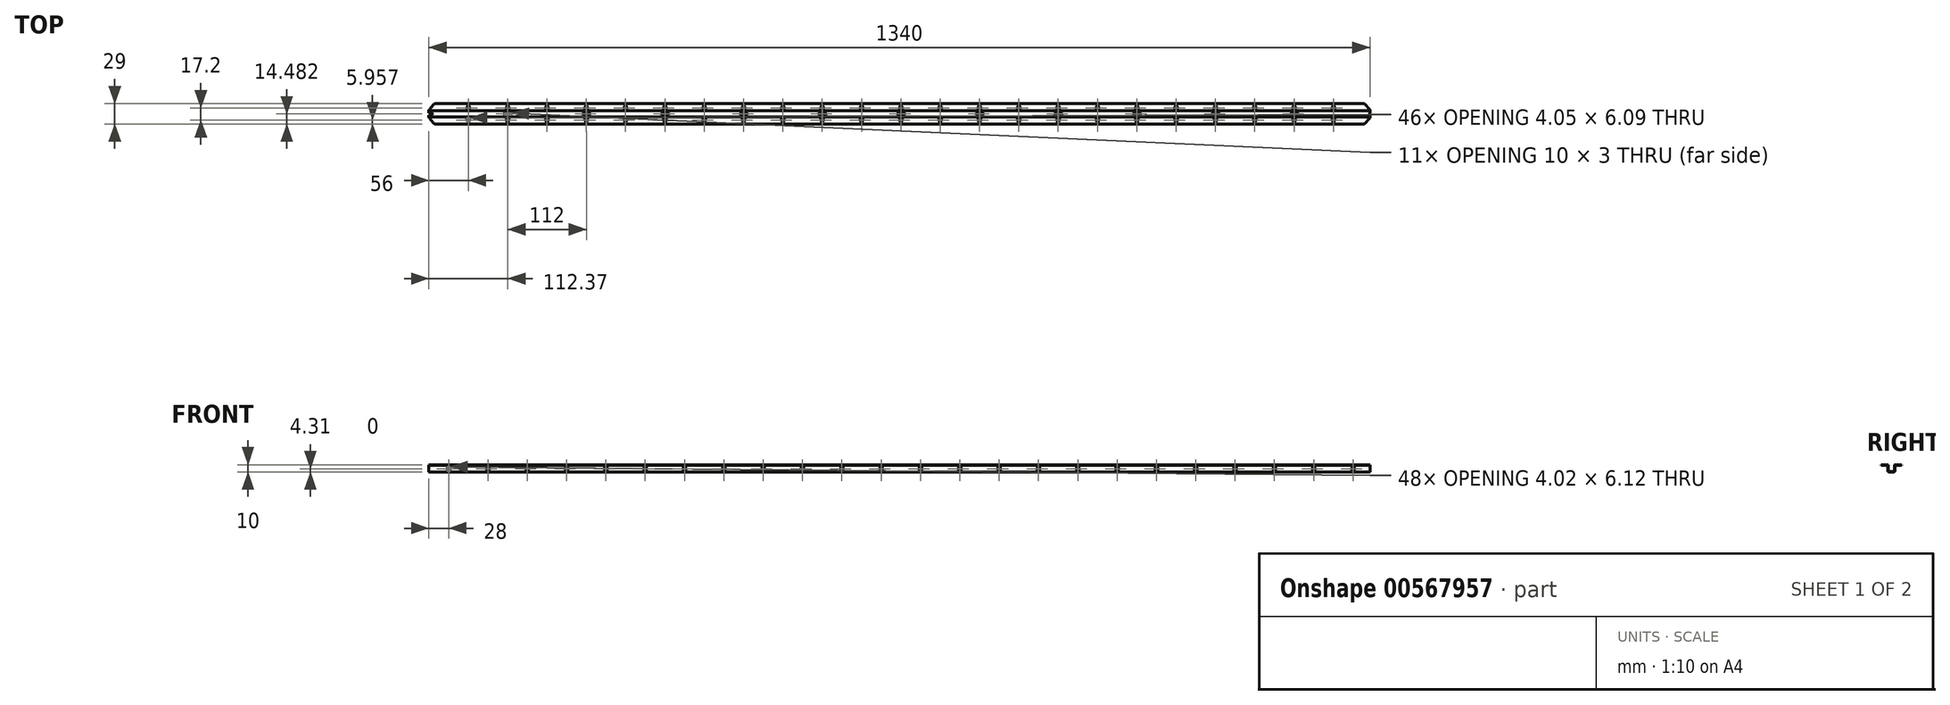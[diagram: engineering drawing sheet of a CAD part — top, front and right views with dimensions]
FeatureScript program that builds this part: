
annotation { "Feature Type Name" : "Feature", "Feature Type Description" : "" }
export const myFeature = defineFeature(function(context is Context, id is Id, definition is map)
    precondition{}
    {
        {
            var Q0;
            Q0=qCreatedBy(makeId("Right.planeOp"),FACE);
            var sketch = newSketch(context, id + "F0", { "sketchPlane" : qUnion([Q0])});
            skLineSegment(sketch, "E0", {"start": v(14.5, 5) * mm, "end": v(5.5, 5) * mm});
            skArc(sketch, "E1", {"start": v(5.5, 5) * mm, "mid": v(4.8, 4.7) * mm, "end": v(4.5, 4) * mm});
            skLineSegment(sketch, "E2", {"start": v(4.5, 4) * mm, "end": v(4.5, -4) * mm});
            skArc(sketch, "E3", {"start": v(4.5, -4) * mm, "mid": v(4.35, -4.35) * mm, "end": v(4, -4.5) * mm});
            skLineSegment(sketch, "E4", {"start": v(4, -4.5) * mm, "end": v(-4, -4.5) * mm});
            skArc(sketch, "E5", {"start": v(-4, -4.5) * mm, "mid": v(-4.35, -4.35) * mm, "end": v(-4.5, -4) * mm});
            skLineSegment(sketch, "E6", {"start": v(-4.5, -4) * mm, "end": v(-4.5, 4) * mm});
            skArc(sketch, "E7", {"start": v(-4.5, 4) * mm, "mid": v(-4.8, 4.7) * mm, "end": v(-5.5, 5) * mm});
            skLineSegment(sketch, "E8", {"start": v(-5.5, 5) * mm, "end": v(-14.5, 5) * mm});
            skLineSegment(sketch, "E9", {"start": v(-14.5, 5) * mm, "end": v(-14.5, 4.5) * mm});
            skLineSegment(sketch, "E10", {"start": v(-14.5, 4.5) * mm, "end": v(-5.5, 4.5) * mm});
            skArc(sketch, "E11", {"start": v(-5.5, 4.5) * mm, "mid": v(-5.15, 4.35) * mm, "end": v(-5, 4) * mm});
            skLineSegment(sketch, "E12", {"start": v(-5, 4) * mm, "end": v(-5, -4) * mm});
            skArc(sketch, "E13", {"start": v(-5, -4) * mm, "mid": v(-4.7, -4.7) * mm, "end": v(-4, -5) * mm});
            skLineSegment(sketch, "E14", {"start": v(-4, -5) * mm, "end": v(4, -5) * mm});
            skArc(sketch, "E15", {"start": v(4, -5) * mm, "mid": v(4.7, -4.7) * mm, "end": v(5, -4) * mm});
            skLineSegment(sketch, "E16", {"start": v(5, -4) * mm, "end": v(5, 4) * mm});
            skArc(sketch, "E17", {"start": v(5, 4) * mm, "mid": v(5.15, 4.35) * mm, "end": v(5.5, 4.5) * mm});
            skLineSegment(sketch, "E18", {"start": v(5.5, 4.5) * mm, "end": v(14.5, 4.5) * mm});
            skLineSegment(sketch, "E19", {"start": v(14.5, 4.5) * mm, "end": v(14.5, 5) * mm});
            skSolve(sketch);
        }
        {
            var Q0;
            Q0 = qSketchRegion(id + "F0", true);
            extrude(context, id + "F1", {"entities" : qUnion([Q0]), "oppositeDirection" : true, "depth" : 1340 * mm, "offsetDistance" : 25 * mm});
        }
        {
            var Q0;
            Q0=makeQuery(id+"F1.opExtrude","SWEPT_FACE",FACE,{"disambiguationData":[OSD([sQuery(id+"F0.wireOp",EDGE,"E4")])]});
            var sketch = newSketch(context, id + "F2", { "sketchPlane" : qUnion([Q0])});
            skLineSegment(sketch, "E20.bottom", {"start": v(-1343.8, -1.5) * mm, "end": v(-1336.2, -1.5) * mm});
            skLineSegment(sketch, "E20.top", {"start": v(-1343.8, 1.5) * mm, "end": v(-1336.2, 1.5) * mm});
            skLineSegment(sketch, "E20.left", {"start": v(-1345, -0.3) * mm, "end": v(-1345, 0.3) * mm});
            skLineSegment(sketch, "E20.right", {"start": v(-1335, -0.3) * mm, "end": v(-1335, 0.3) * mm});
            skArc(sketch, "E21.filletArc", {"start": v(-1345, -0.3) * mm, "mid": v(-1344.65, -1.15) * mm, "end": v(-1343.8, -1.5) * mm});
            skArc(sketch, "E22.filletArc", {"start": v(-1343.8, 1.5) * mm, "mid": v(-1344.65, 1.15) * mm, "end": v(-1345, 0.3) * mm});
            skArc(sketch, "E23.filletArc", {"start": v(-1335, 0.3) * mm, "mid": v(-1335.35, 1.15) * mm, "end": v(-1336.2, 1.5) * mm});
            skArc(sketch, "E24.filletArc", {"start": v(-1336.2, -1.5) * mm, "mid": v(-1335.35, -1.15) * mm, "end": v(-1335, -0.3) * mm});
            skLineSegment(sketch, "E25.bottom", {"start": v(-1119.43, -1.52) * mm, "end": v(-1111.83, -1.52) * mm});
            skLineSegment(sketch, "E25.top", {"start": v(-1119.43, 1.48) * mm, "end": v(-1111.83, 1.48) * mm});
            skLineSegment(sketch, "E25.left", {"start": v(-1120.63, -0.32) * mm, "end": v(-1120.63, 0.28) * mm});
            skLineSegment(sketch, "E25.right", {"start": v(-1110.63, -0.32) * mm, "end": v(-1110.63, 0.28) * mm});
            skArc(sketch, "E26.filletArc", {"start": v(-1120.63, -0.32) * mm, "mid": v(-1120.28, -1.17) * mm, "end": v(-1119.43, -1.52) * mm});
            skArc(sketch, "E27.filletArc", {"start": v(-1119.43, 1.48) * mm, "mid": v(-1120.28, 1.13) * mm, "end": v(-1120.63, 0.28) * mm});
            skArc(sketch, "E28.filletArc", {"start": v(-1110.63, 0.28) * mm, "mid": v(-1110.98, 1.13) * mm, "end": v(-1111.83, 1.48) * mm});
            skArc(sketch, "E29.filletArc", {"start": v(-1111.83, -1.52) * mm, "mid": v(-1110.98, -1.17) * mm, "end": v(-1110.63, -0.32) * mm});
            skLineSegment(sketch, "E30.bottom", {"start": v(-1231.43, -1.52) * mm, "end": v(-1223.83, -1.52) * mm});
            skLineSegment(sketch, "E30.top", {"start": v(-1231.43, 1.48) * mm, "end": v(-1223.83, 1.48) * mm});
            skLineSegment(sketch, "E30.left", {"start": v(-1232.63, -0.32) * mm, "end": v(-1232.63, 0.28) * mm});
            skLineSegment(sketch, "E30.right", {"start": v(-1222.63, -0.32) * mm, "end": v(-1222.63, 0.28) * mm});
            skArc(sketch, "E31.filletArc", {"start": v(-1232.63, -0.32) * mm, "mid": v(-1232.28, -1.17) * mm, "end": v(-1231.43, -1.52) * mm});
            skArc(sketch, "E32.filletArc", {"start": v(-1231.43, 1.48) * mm, "mid": v(-1232.28, 1.13) * mm, "end": v(-1232.63, 0.28) * mm});
            skArc(sketch, "E33.filletArc", {"start": v(-1222.63, 0.28) * mm, "mid": v(-1222.98, 1.13) * mm, "end": v(-1223.83, 1.48) * mm});
            skArc(sketch, "E34.filletArc", {"start": v(-1223.83, -1.52) * mm, "mid": v(-1222.98, -1.17) * mm, "end": v(-1222.63, -0.32) * mm});
            skLineSegment(sketch, "E35.bottom", {"start": v(-1007.43, -1.52) * mm, "end": v(-999.83, -1.52) * mm});
            skLineSegment(sketch, "E35.top", {"start": v(-1007.43, 1.48) * mm, "end": v(-999.83, 1.48) * mm});
            skLineSegment(sketch, "E35.left", {"start": v(-1008.63, -0.32) * mm, "end": v(-1008.63, 0.28) * mm});
            skLineSegment(sketch, "E35.right", {"start": v(-998.63, -0.32) * mm, "end": v(-998.63, 0.28) * mm});
            skArc(sketch, "E36.filletArc", {"start": v(-1008.63, -0.32) * mm, "mid": v(-1008.28, -1.17) * mm, "end": v(-1007.43, -1.52) * mm});
            skArc(sketch, "E37.filletArc", {"start": v(-1007.43, 1.48) * mm, "mid": v(-1008.28, 1.13) * mm, "end": v(-1008.63, 0.28) * mm});
            skArc(sketch, "E38.filletArc", {"start": v(-998.63, 0.28) * mm, "mid": v(-998.98, 1.13) * mm, "end": v(-999.83, 1.48) * mm});
            skArc(sketch, "E39.filletArc", {"start": v(-999.83, -1.52) * mm, "mid": v(-998.98, -1.17) * mm, "end": v(-998.63, -0.32) * mm});
            skLineSegment(sketch, "E40.1.0.0", {"start": v(-895.43, -1.52) * mm, "end": v(-887.83, -1.52) * mm});
            skArc(sketch, "E40.1.0.1", {"start": v(-896.63, -0.32) * mm, "mid": v(-896.28, -1.17) * mm, "end": v(-895.43, -1.52) * mm});
            skLineSegment(sketch, "E40.1.0.2", {"start": v(-896.63, -0.32) * mm, "end": v(-896.63, 0.28) * mm});
            skArc(sketch, "E40.1.0.3", {"start": v(-895.43, 1.48) * mm, "mid": v(-896.28, 1.13) * mm, "end": v(-896.63, 0.28) * mm});
            skLineSegment(sketch, "E40.1.0.4", {"start": v(-895.43, 1.48) * mm, "end": v(-887.83, 1.48) * mm});
            skArc(sketch, "E40.1.0.5", {"start": v(-886.63, 0.28) * mm, "mid": v(-886.98, 1.13) * mm, "end": v(-887.83, 1.48) * mm});
            skLineSegment(sketch, "E40.1.0.6", {"start": v(-886.63, -0.32) * mm, "end": v(-886.63, 0.28) * mm});
            skArc(sketch, "E40.1.0.7", {"start": v(-887.83, -1.52) * mm, "mid": v(-886.98, -1.17) * mm, "end": v(-886.63, -0.32) * mm});
            skLineSegment(sketch, "E40.2.0.0", {"start": v(-783.43, -1.52) * mm, "end": v(-775.83, -1.52) * mm});
            skArc(sketch, "E40.2.0.1", {"start": v(-784.63, -0.32) * mm, "mid": v(-784.28, -1.17) * mm, "end": v(-783.43, -1.52) * mm});
            skLineSegment(sketch, "E40.2.0.2", {"start": v(-784.63, -0.32) * mm, "end": v(-784.63, 0.28) * mm});
            skArc(sketch, "E40.2.0.3", {"start": v(-783.43, 1.48) * mm, "mid": v(-784.28, 1.13) * mm, "end": v(-784.63, 0.28) * mm});
            skLineSegment(sketch, "E40.2.0.4", {"start": v(-783.43, 1.48) * mm, "end": v(-775.83, 1.48) * mm});
            skArc(sketch, "E40.2.0.5", {"start": v(-774.63, 0.28) * mm, "mid": v(-774.98, 1.13) * mm, "end": v(-775.83, 1.48) * mm});
            skLineSegment(sketch, "E40.2.0.6", {"start": v(-774.63, -0.32) * mm, "end": v(-774.63, 0.28) * mm});
            skArc(sketch, "E40.2.0.7", {"start": v(-775.83, -1.52) * mm, "mid": v(-774.98, -1.17) * mm, "end": v(-774.63, -0.32) * mm});
            skLineSegment(sketch, "E40.3.0.0", {"start": v(-671.43, -1.52) * mm, "end": v(-663.83, -1.52) * mm});
            skArc(sketch, "E40.3.0.1", {"start": v(-672.63, -0.32) * mm, "mid": v(-672.28, -1.17) * mm, "end": v(-671.43, -1.52) * mm});
            skLineSegment(sketch, "E40.3.0.2", {"start": v(-672.63, -0.32) * mm, "end": v(-672.63, 0.28) * mm});
            skArc(sketch, "E40.3.0.3", {"start": v(-671.43, 1.48) * mm, "mid": v(-672.28, 1.13) * mm, "end": v(-672.63, 0.28) * mm});
            skLineSegment(sketch, "E40.3.0.4", {"start": v(-671.43, 1.48) * mm, "end": v(-663.83, 1.48) * mm});
            skArc(sketch, "E40.3.0.5", {"start": v(-662.63, 0.28) * mm, "mid": v(-662.98, 1.13) * mm, "end": v(-663.83, 1.48) * mm});
            skLineSegment(sketch, "E40.3.0.6", {"start": v(-662.63, -0.32) * mm, "end": v(-662.63, 0.28) * mm});
            skArc(sketch, "E40.3.0.7", {"start": v(-663.83, -1.52) * mm, "mid": v(-662.98, -1.17) * mm, "end": v(-662.63, -0.32) * mm});
            skLineSegment(sketch, "E40.4.0.0", {"start": v(-559.43, -1.52) * mm, "end": v(-551.83, -1.52) * mm});
            skArc(sketch, "E40.4.0.1", {"start": v(-560.63, -0.32) * mm, "mid": v(-560.28, -1.17) * mm, "end": v(-559.43, -1.52) * mm});
            skLineSegment(sketch, "E40.4.0.2", {"start": v(-560.63, -0.32) * mm, "end": v(-560.63, 0.28) * mm});
            skArc(sketch, "E40.4.0.3", {"start": v(-559.43, 1.48) * mm, "mid": v(-560.28, 1.13) * mm, "end": v(-560.63, 0.28) * mm});
            skLineSegment(sketch, "E40.4.0.4", {"start": v(-559.43, 1.48) * mm, "end": v(-551.83, 1.48) * mm});
            skArc(sketch, "E40.4.0.5", {"start": v(-550.63, 0.28) * mm, "mid": v(-550.98, 1.13) * mm, "end": v(-551.83, 1.48) * mm});
            skLineSegment(sketch, "E40.4.0.6", {"start": v(-550.63, -0.32) * mm, "end": v(-550.63, 0.28) * mm});
            skArc(sketch, "E40.4.0.7", {"start": v(-551.83, -1.52) * mm, "mid": v(-550.98, -1.17) * mm, "end": v(-550.63, -0.32) * mm});
            skLineSegment(sketch, "E40.5.0.0", {"start": v(-447.43, -1.52) * mm, "end": v(-439.83, -1.52) * mm});
            skArc(sketch, "E40.5.0.1", {"start": v(-448.63, -0.32) * mm, "mid": v(-448.28, -1.17) * mm, "end": v(-447.43, -1.52) * mm});
            skLineSegment(sketch, "E40.5.0.2", {"start": v(-448.63, -0.32) * mm, "end": v(-448.63, 0.28) * mm});
            skArc(sketch, "E40.5.0.3", {"start": v(-447.43, 1.48) * mm, "mid": v(-448.28, 1.13) * mm, "end": v(-448.63, 0.28) * mm});
            skLineSegment(sketch, "E40.5.0.4", {"start": v(-447.43, 1.48) * mm, "end": v(-439.83, 1.48) * mm});
            skArc(sketch, "E40.5.0.5", {"start": v(-438.63, 0.28) * mm, "mid": v(-438.98, 1.13) * mm, "end": v(-439.83, 1.48) * mm});
            skLineSegment(sketch, "E40.5.0.6", {"start": v(-438.63, -0.32) * mm, "end": v(-438.63, 0.28) * mm});
            skArc(sketch, "E40.5.0.7", {"start": v(-439.83, -1.52) * mm, "mid": v(-438.98, -1.17) * mm, "end": v(-438.63, -0.32) * mm});
            skLineSegment(sketch, "E40.6.0.0", {"start": v(-335.43, -1.52) * mm, "end": v(-327.83, -1.52) * mm});
            skArc(sketch, "E40.6.0.1", {"start": v(-336.63, -0.32) * mm, "mid": v(-336.28, -1.17) * mm, "end": v(-335.43, -1.52) * mm});
            skLineSegment(sketch, "E40.6.0.2", {"start": v(-336.63, -0.32) * mm, "end": v(-336.63, 0.28) * mm});
            skArc(sketch, "E40.6.0.3", {"start": v(-335.43, 1.48) * mm, "mid": v(-336.28, 1.13) * mm, "end": v(-336.63, 0.28) * mm});
            skLineSegment(sketch, "E40.6.0.4", {"start": v(-335.43, 1.48) * mm, "end": v(-327.83, 1.48) * mm});
            skArc(sketch, "E40.6.0.5", {"start": v(-326.63, 0.28) * mm, "mid": v(-326.98, 1.13) * mm, "end": v(-327.83, 1.48) * mm});
            skLineSegment(sketch, "E40.6.0.6", {"start": v(-326.63, -0.32) * mm, "end": v(-326.63, 0.28) * mm});
            skArc(sketch, "E40.6.0.7", {"start": v(-327.83, -1.52) * mm, "mid": v(-326.98, -1.17) * mm, "end": v(-326.63, -0.32) * mm});
            skLineSegment(sketch, "E40.7.0.0", {"start": v(-223.43, -1.52) * mm, "end": v(-215.83, -1.52) * mm});
            skArc(sketch, "E40.7.0.1", {"start": v(-224.63, -0.32) * mm, "mid": v(-224.28, -1.17) * mm, "end": v(-223.43, -1.52) * mm});
            skLineSegment(sketch, "E40.7.0.2", {"start": v(-224.63, -0.32) * mm, "end": v(-224.63, 0.28) * mm});
            skArc(sketch, "E40.7.0.3", {"start": v(-223.43, 1.48) * mm, "mid": v(-224.28, 1.13) * mm, "end": v(-224.63, 0.28) * mm});
            skLineSegment(sketch, "E40.7.0.4", {"start": v(-223.43, 1.48) * mm, "end": v(-215.83, 1.48) * mm});
            skArc(sketch, "E40.7.0.5", {"start": v(-214.63, 0.28) * mm, "mid": v(-214.98, 1.13) * mm, "end": v(-215.83, 1.48) * mm});
            skLineSegment(sketch, "E40.7.0.6", {"start": v(-214.63, -0.32) * mm, "end": v(-214.63, 0.28) * mm});
            skArc(sketch, "E40.7.0.7", {"start": v(-215.83, -1.52) * mm, "mid": v(-214.98, -1.17) * mm, "end": v(-214.63, -0.32) * mm});
            skLineSegment(sketch, "E40.8.0.0", {"start": v(-111.43, -1.52) * mm, "end": v(-103.83, -1.52) * mm});
            skArc(sketch, "E40.8.0.1", {"start": v(-112.63, -0.32) * mm, "mid": v(-112.28, -1.17) * mm, "end": v(-111.43, -1.52) * mm});
            skLineSegment(sketch, "E40.8.0.2", {"start": v(-112.63, -0.32) * mm, "end": v(-112.63, 0.28) * mm});
            skArc(sketch, "E40.8.0.3", {"start": v(-111.43, 1.48) * mm, "mid": v(-112.28, 1.13) * mm, "end": v(-112.63, 0.28) * mm});
            skLineSegment(sketch, "E40.8.0.4", {"start": v(-111.43, 1.48) * mm, "end": v(-103.83, 1.48) * mm});
            skArc(sketch, "E40.8.0.5", {"start": v(-102.63, 0.28) * mm, "mid": v(-102.98, 1.13) * mm, "end": v(-103.83, 1.48) * mm});
            skLineSegment(sketch, "E40.8.0.6", {"start": v(-102.63, -0.32) * mm, "end": v(-102.63, 0.28) * mm});
            skArc(sketch, "E40.8.0.7", {"start": v(-103.83, -1.52) * mm, "mid": v(-102.98, -1.17) * mm, "end": v(-102.63, -0.32) * mm});
            skLineSegment(sketch, "E40.9.0.0", {"start": v(0.57, -1.52) * mm, "end": v(8.17, -1.52) * mm});
            skArc(sketch, "E40.9.0.1", {"start": v(-0.63, -0.32) * mm, "mid": v(-0.28, -1.17) * mm, "end": v(0.57, -1.52) * mm});
            skLineSegment(sketch, "E40.9.0.2", {"start": v(-0.63, -0.32) * mm, "end": v(-0.63, 0.28) * mm});
            skArc(sketch, "E40.9.0.3", {"start": v(0.57, 1.48) * mm, "mid": v(-0.28, 1.13) * mm, "end": v(-0.63, 0.28) * mm});
            skLineSegment(sketch, "E40.9.0.4", {"start": v(0.57, 1.48) * mm, "end": v(8.17, 1.48) * mm});
            skArc(sketch, "E40.9.0.5", {"start": v(9.37, 0.28) * mm, "mid": v(9.02, 1.13) * mm, "end": v(8.17, 1.48) * mm});
            skLineSegment(sketch, "E40.9.0.6", {"start": v(9.37, -0.32) * mm, "end": v(9.37, 0.28) * mm});
            skArc(sketch, "E40.9.0.7", {"start": v(8.17, -1.52) * mm, "mid": v(9.02, -1.17) * mm, "end": v(9.37, -0.32) * mm});
            skLineSegment(sketch, "E40.direction1", {"start": v(-998.63, -0.32) * mm, "end": v(-886.63, -0.32) * mm, "construction": true});
            skSolve(sketch);
        }
        {
            var Q0;
            Q0 = qSketchRegion(id + "F2", true);
            extrude(context, id + "F3", {"entities" : qUnion([Q0]), "operationType" : NewBodyOperationType.REMOVE, "endBound" : BoundingType.THROUGH_ALL, "oppositeDirection" : true, "depth" : 25 * mm, "offsetDistance" : 25 * mm});
        }
        {
            var Q0;
            Q0=makeQuery(id+"F1.opExtrude","SWEPT_FACE",FACE,{"disambiguationData":[OSD([sQuery(id+"F0.wireOp",EDGE,"E12")])]});
            var sketch = newSketch(context, id + "F4", { "sketchPlane" : qUnion([Q0])});
            skEllipse(sketch, "E41", {"center": v(-1312, -0.69) * mm, "majorRadius": 3.06 * mm, "minorRadius": 2.01 * mm, "majorAxis": v(0, 1)});
            skEllipse(sketch, "E42.1.0.0", {"center": v(-1256, -0.69) * mm, "majorRadius": 3.06 * mm, "minorRadius": 2.01 * mm, "majorAxis": v(0, 1)});
            skEllipse(sketch, "E42.2.0.0", {"center": v(-1200, -0.69) * mm, "majorRadius": 3.06 * mm, "minorRadius": 2.01 * mm, "majorAxis": v(0, 1)});
            skEllipse(sketch, "E42.3.0.0", {"center": v(-1144, -0.69) * mm, "majorRadius": 3.06 * mm, "minorRadius": 2.01 * mm, "majorAxis": v(0, 1)});
            skEllipse(sketch, "E42.4.0.0", {"center": v(-1088, -0.69) * mm, "majorRadius": 3.06 * mm, "minorRadius": 2.01 * mm, "majorAxis": v(0, 1)});
            skEllipse(sketch, "E42.5.0.0", {"center": v(-1032, -0.69) * mm, "majorRadius": 3.06 * mm, "minorRadius": 2.01 * mm, "majorAxis": v(0, 1)});
            skEllipse(sketch, "E42.6.0.0", {"center": v(-976, -0.69) * mm, "majorRadius": 3.06 * mm, "minorRadius": 2.01 * mm, "majorAxis": v(0, 1)});
            skEllipse(sketch, "E42.7.0.0", {"center": v(-920, -0.69) * mm, "majorRadius": 3.06 * mm, "minorRadius": 2.01 * mm, "majorAxis": v(0, 1)});
            skEllipse(sketch, "E42.8.0.0", {"center": v(-864, -0.69) * mm, "majorRadius": 3.06 * mm, "minorRadius": 2.01 * mm, "majorAxis": v(0, 1)});
            skEllipse(sketch, "E42.9.0.0", {"center": v(-808, -0.69) * mm, "majorRadius": 3.06 * mm, "minorRadius": 2.01 * mm, "majorAxis": v(0, 1)});
            skEllipse(sketch, "E42.10.0.0", {"center": v(-752, -0.69) * mm, "majorRadius": 3.06 * mm, "minorRadius": 2.01 * mm, "majorAxis": v(0, 1)});
            skEllipse(sketch, "E42.11.0.0", {"center": v(-696, -0.69) * mm, "majorRadius": 3.06 * mm, "minorRadius": 2.01 * mm, "majorAxis": v(0, 1)});
            skEllipse(sketch, "E42.12.0.0", {"center": v(-640, -0.69) * mm, "majorRadius": 3.06 * mm, "minorRadius": 2.01 * mm, "majorAxis": v(0, 1)});
            skEllipse(sketch, "E42.13.0.0", {"center": v(-584, -0.69) * mm, "majorRadius": 3.06 * mm, "minorRadius": 2.01 * mm, "majorAxis": v(0, 1)});
            skEllipse(sketch, "E42.14.0.0", {"center": v(-528, -0.69) * mm, "majorRadius": 3.06 * mm, "minorRadius": 2.01 * mm, "majorAxis": v(0, 1)});
            skEllipse(sketch, "E42.15.0.0", {"center": v(-472, -0.69) * mm, "majorRadius": 3.06 * mm, "minorRadius": 2.01 * mm, "majorAxis": v(0, 1)});
            skEllipse(sketch, "E42.16.0.0", {"center": v(-416, -0.69) * mm, "majorRadius": 3.06 * mm, "minorRadius": 2.01 * mm, "majorAxis": v(0, 1)});
            skEllipse(sketch, "E42.17.0.0", {"center": v(-360, -0.69) * mm, "majorRadius": 3.06 * mm, "minorRadius": 2.01 * mm, "majorAxis": v(0, 1)});
            skEllipse(sketch, "E42.18.0.0", {"center": v(-304, -0.69) * mm, "majorRadius": 3.06 * mm, "minorRadius": 2.01 * mm, "majorAxis": v(0, 1)});
            skEllipse(sketch, "E42.19.0.0", {"center": v(-248, -0.69) * mm, "majorRadius": 3.06 * mm, "minorRadius": 2.01 * mm, "majorAxis": v(0, 1)});
            skEllipse(sketch, "E42.20.0.0", {"center": v(-192, -0.69) * mm, "majorRadius": 3.06 * mm, "minorRadius": 2.01 * mm, "majorAxis": v(0, 1)});
            skEllipse(sketch, "E42.21.0.0", {"center": v(-136, -0.69) * mm, "majorRadius": 3.06 * mm, "minorRadius": 2.01 * mm, "majorAxis": v(0, 1)});
            skEllipse(sketch, "E42.22.0.0", {"center": v(-80, -0.69) * mm, "majorRadius": 3.06 * mm, "minorRadius": 2.01 * mm, "majorAxis": v(0, 1)});
            skEllipse(sketch, "E42.23.0.0", {"center": v(-24, -0.69) * mm, "majorRadius": 3.06 * mm, "minorRadius": 2.01 * mm, "majorAxis": v(0, 1)});
            skLineSegment(sketch, "E42.direction1", {"start": v(-1340, -0.69) * mm, "end": v(-1284, -0.69) * mm, "construction": true});
            skSolve(sketch);
        }
        {
            var Q0;
            Q0 = qSketchRegion(id + "F4", true);
            extrude(context, id + "F5", {"entities" : qUnion([Q0]), "operationType" : NewBodyOperationType.REMOVE, "oppositeDirection" : true, "depth" : 15 * mm, "offsetDistance" : 25 * mm});
        }
        {
            var Q0;
            Q0=makeQuery(id+"F1.opExtrude","SWEPT_FACE",FACE,{"disambiguationData":[OSD([sQuery(id+"F0.wireOp",EDGE,"E8")])]});
            var sketch = newSketch(context, id + "F6", { "sketchPlane" : qUnion([Q0])});
            skEllipse(sketch, "E43", {"center": v(-1340, -8.54) * mm, "majorRadius": 3.04 * mm, "minorRadius": 2.03 * mm, "majorAxis": v(0, -1)});
            skEllipse(sketch, "E44.0.1.0", {"center": v(-1340, 8.66) * mm, "majorRadius": 3.04 * mm, "minorRadius": 2.03 * mm, "majorAxis": v(0, -1)});
            skEllipse(sketch, "E44.1.0.0", {"center": v(-1284, -8.54) * mm, "majorRadius": 3.04 * mm, "minorRadius": 2.03 * mm, "majorAxis": v(0, -1)});
            skEllipse(sketch, "E44.1.1.0", {"center": v(-1284, 8.66) * mm, "majorRadius": 3.04 * mm, "minorRadius": 2.03 * mm, "majorAxis": v(0, -1)});
            skEllipse(sketch, "E44.2.0.0", {"center": v(-1228, -8.54) * mm, "majorRadius": 3.04 * mm, "minorRadius": 2.03 * mm, "majorAxis": v(0, -1)});
            skEllipse(sketch, "E44.2.1.0", {"center": v(-1228, 8.66) * mm, "majorRadius": 3.04 * mm, "minorRadius": 2.03 * mm, "majorAxis": v(0, -1)});
            skEllipse(sketch, "E44.3.0.0", {"center": v(-1172, -8.54) * mm, "majorRadius": 3.04 * mm, "minorRadius": 2.03 * mm, "majorAxis": v(0, -1)});
            skEllipse(sketch, "E44.3.1.0", {"center": v(-1172, 8.66) * mm, "majorRadius": 3.04 * mm, "minorRadius": 2.03 * mm, "majorAxis": v(0, -1)});
            skEllipse(sketch, "E44.4.0.0", {"center": v(-1116, -8.54) * mm, "majorRadius": 3.04 * mm, "minorRadius": 2.03 * mm, "majorAxis": v(0, -1)});
            skEllipse(sketch, "E44.4.1.0", {"center": v(-1116, 8.66) * mm, "majorRadius": 3.04 * mm, "minorRadius": 2.03 * mm, "majorAxis": v(0, -1)});
            skEllipse(sketch, "E44.5.0.0", {"center": v(-1060, -8.54) * mm, "majorRadius": 3.04 * mm, "minorRadius": 2.03 * mm, "majorAxis": v(0, -1)});
            skEllipse(sketch, "E44.5.1.0", {"center": v(-1060, 8.66) * mm, "majorRadius": 3.04 * mm, "minorRadius": 2.03 * mm, "majorAxis": v(0, -1)});
            skEllipse(sketch, "E44.6.0.0", {"center": v(-1004, -8.54) * mm, "majorRadius": 3.04 * mm, "minorRadius": 2.03 * mm, "majorAxis": v(0, -1)});
            skEllipse(sketch, "E44.6.1.0", {"center": v(-1004, 8.66) * mm, "majorRadius": 3.04 * mm, "minorRadius": 2.03 * mm, "majorAxis": v(0, -1)});
            skEllipse(sketch, "E44.7.0.0", {"center": v(-948, -8.54) * mm, "majorRadius": 3.04 * mm, "minorRadius": 2.03 * mm, "majorAxis": v(0, -1)});
            skEllipse(sketch, "E44.7.1.0", {"center": v(-948, 8.66) * mm, "majorRadius": 3.04 * mm, "minorRadius": 2.03 * mm, "majorAxis": v(0, -1)});
            skEllipse(sketch, "E44.8.0.0", {"center": v(-892, -8.54) * mm, "majorRadius": 3.04 * mm, "minorRadius": 2.03 * mm, "majorAxis": v(0, -1)});
            skEllipse(sketch, "E44.8.1.0", {"center": v(-892, 8.66) * mm, "majorRadius": 3.04 * mm, "minorRadius": 2.03 * mm, "majorAxis": v(0, -1)});
            skEllipse(sketch, "E44.9.0.0", {"center": v(-836, -8.54) * mm, "majorRadius": 3.04 * mm, "minorRadius": 2.03 * mm, "majorAxis": v(0, -1)});
            skEllipse(sketch, "E44.9.1.0", {"center": v(-836, 8.66) * mm, "majorRadius": 3.04 * mm, "minorRadius": 2.03 * mm, "majorAxis": v(0, -1)});
            skEllipse(sketch, "E44.10.0.0", {"center": v(-780, -8.54) * mm, "majorRadius": 3.04 * mm, "minorRadius": 2.03 * mm, "majorAxis": v(0, -1)});
            skEllipse(sketch, "E44.10.1.0", {"center": v(-780, 8.66) * mm, "majorRadius": 3.04 * mm, "minorRadius": 2.03 * mm, "majorAxis": v(0, -1)});
            skEllipse(sketch, "E44.11.0.0", {"center": v(-724, -8.54) * mm, "majorRadius": 3.04 * mm, "minorRadius": 2.03 * mm, "majorAxis": v(0, -1)});
            skEllipse(sketch, "E44.11.1.0", {"center": v(-724, 8.66) * mm, "majorRadius": 3.04 * mm, "minorRadius": 2.03 * mm, "majorAxis": v(0, -1)});
            skEllipse(sketch, "E44.12.0.0", {"center": v(-668, -8.54) * mm, "majorRadius": 3.04 * mm, "minorRadius": 2.03 * mm, "majorAxis": v(0, -1)});
            skEllipse(sketch, "E44.12.1.0", {"center": v(-668, 8.66) * mm, "majorRadius": 3.04 * mm, "minorRadius": 2.03 * mm, "majorAxis": v(0, -1)});
            skEllipse(sketch, "E44.13.0.0", {"center": v(-612, -8.54) * mm, "majorRadius": 3.04 * mm, "minorRadius": 2.03 * mm, "majorAxis": v(0, -1)});
            skEllipse(sketch, "E44.13.1.0", {"center": v(-612, 8.66) * mm, "majorRadius": 3.04 * mm, "minorRadius": 2.03 * mm, "majorAxis": v(0, -1)});
            skEllipse(sketch, "E44.14.0.0", {"center": v(-556, -8.54) * mm, "majorRadius": 3.04 * mm, "minorRadius": 2.03 * mm, "majorAxis": v(0, -1)});
            skEllipse(sketch, "E44.14.1.0", {"center": v(-556, 8.66) * mm, "majorRadius": 3.04 * mm, "minorRadius": 2.03 * mm, "majorAxis": v(0, -1)});
            skEllipse(sketch, "E44.15.0.0", {"center": v(-500, -8.54) * mm, "majorRadius": 3.04 * mm, "minorRadius": 2.03 * mm, "majorAxis": v(0, -1)});
            skEllipse(sketch, "E44.15.1.0", {"center": v(-500, 8.66) * mm, "majorRadius": 3.04 * mm, "minorRadius": 2.03 * mm, "majorAxis": v(0, -1)});
            skEllipse(sketch, "E44.16.0.0", {"center": v(-444, -8.54) * mm, "majorRadius": 3.04 * mm, "minorRadius": 2.03 * mm, "majorAxis": v(0, -1)});
            skEllipse(sketch, "E44.16.1.0", {"center": v(-444, 8.66) * mm, "majorRadius": 3.04 * mm, "minorRadius": 2.03 * mm, "majorAxis": v(0, -1)});
            skEllipse(sketch, "E44.17.0.0", {"center": v(-388, -8.54) * mm, "majorRadius": 3.04 * mm, "minorRadius": 2.03 * mm, "majorAxis": v(0, -1)});
            skEllipse(sketch, "E44.17.1.0", {"center": v(-388, 8.66) * mm, "majorRadius": 3.04 * mm, "minorRadius": 2.03 * mm, "majorAxis": v(0, -1)});
            skEllipse(sketch, "E44.18.0.0", {"center": v(-332, -8.54) * mm, "majorRadius": 3.04 * mm, "minorRadius": 2.03 * mm, "majorAxis": v(0, -1)});
            skEllipse(sketch, "E44.18.1.0", {"center": v(-332, 8.66) * mm, "majorRadius": 3.04 * mm, "minorRadius": 2.03 * mm, "majorAxis": v(0, -1)});
            skEllipse(sketch, "E44.19.0.0", {"center": v(-276, -8.54) * mm, "majorRadius": 3.04 * mm, "minorRadius": 2.03 * mm, "majorAxis": v(0, -1)});
            skEllipse(sketch, "E44.19.1.0", {"center": v(-276, 8.66) * mm, "majorRadius": 3.04 * mm, "minorRadius": 2.03 * mm, "majorAxis": v(0, -1)});
            skEllipse(sketch, "E44.20.0.0", {"center": v(-220, -8.54) * mm, "majorRadius": 3.04 * mm, "minorRadius": 2.03 * mm, "majorAxis": v(0, -1)});
            skEllipse(sketch, "E44.20.1.0", {"center": v(-220, 8.66) * mm, "majorRadius": 3.04 * mm, "minorRadius": 2.03 * mm, "majorAxis": v(0, -1)});
            skEllipse(sketch, "E44.21.0.0", {"center": v(-164, -8.54) * mm, "majorRadius": 3.04 * mm, "minorRadius": 2.03 * mm, "majorAxis": v(0, -1)});
            skEllipse(sketch, "E44.21.1.0", {"center": v(-164, 8.66) * mm, "majorRadius": 3.04 * mm, "minorRadius": 2.03 * mm, "majorAxis": v(0, -1)});
            skEllipse(sketch, "E44.22.0.0", {"center": v(-108, -8.54) * mm, "majorRadius": 3.04 * mm, "minorRadius": 2.03 * mm, "majorAxis": v(0, -1)});
            skEllipse(sketch, "E44.22.1.0", {"center": v(-108, 8.66) * mm, "majorRadius": 3.04 * mm, "minorRadius": 2.03 * mm, "majorAxis": v(0, -1)});
            skEllipse(sketch, "E44.23.0.0", {"center": v(-52, -8.54) * mm, "majorRadius": 3.04 * mm, "minorRadius": 2.03 * mm, "majorAxis": v(0, -1)});
            skEllipse(sketch, "E44.23.1.0", {"center": v(-52, 8.66) * mm, "majorRadius": 3.04 * mm, "minorRadius": 2.03 * mm, "majorAxis": v(0, -1)});
            skLineSegment(sketch, "E44.direction1", {"start": v(-1340, -8.54) * mm, "end": v(-1284, -8.54) * mm, "construction": true});
            skLineSegment(sketch, "E44.direction2", {"start": v(-1340, -8.54) * mm, "end": v(-1340, 8.66) * mm, "construction": true});
            skSolve(sketch);
        }
        {
            var Q0;
            Q0 = qSketchRegion(id + "F6", true);
            extrude(context, id + "F7", {"entities" : qUnion([Q0]), "operationType" : NewBodyOperationType.REMOVE, "endBound" : BoundingType.THROUGH_ALL, "oppositeDirection" : true, "depth" : 25 * mm, "offsetDistance" : 25 * mm});
        }
        {
            var Q0;
            Q0=makeQuery(id+"F1.opExtrude","SWEPT_FACE",FACE,{"disambiguationData":[OSD([sQuery(id+"F0.wireOp",EDGE,"E0")])]});
            var sketch = newSketch(context, id + "F8", { "sketchPlane" : qUnion([Q0])});
            skLineSegment(sketch, "E45", {"start": v(0, 5.5) * mm, "end": v(-8.13, 14.5) * mm});
            skLineSegment(sketch, "E46", {"start": v(-1340, 5.5) * mm, "end": v(-1331.83, 14.5) * mm});
            skSolve(sketch);
        }
        {
            var Q0;
            {var subQ0=sQuery(id+"F8.wireOp",EDGE,"E46");var subQ5=sQuery(id+"F6.wireOp",EDGE,"E44.0.1.0");var subQ6=makeQuery(id+"F7.boolean.opBoolean","COPY",EDGE,{"derivedFrom":makeQuery(id+"F7.opExtrude","CAP_EDGE",EDGE,{"disambiguationData":[OSD([subQ5])],"isStart":true})});var subQ7=makeQuery(id+"F8.imprint","INTERSECT",VERTEX,{"disambiguationData":[OD(1.0)],"derivedFrom":[subQ6,subQ0]});Q0=makeQuery(id+"F8.imprint","IMPRINT",FACE,{"disambiguationData":[TD([[makeQuery(id+"F8.imprint","IMPRINT",EDGE,{"disambiguationData":[TD([[subQ7,-1.0]])],"derivedFrom":subQ0}),1.0]])]});}
            var Q1;
            {var subQ0=sQuery(id+"F8.wireOp",EDGE,"E45");Q1=makeQuery(id+"F8.imprint","IMPRINT",FACE,{"disambiguationData":[TD([[makeQuery(id+"F8.imprint","IMPRINT",EDGE,{"derivedFrom":subQ0}),-1.0]])]});}
            extrude(context, id + "F9", {"entities" : qUnion([Q0, Q1]), "operationType" : NewBodyOperationType.REMOVE, "endBound" : BoundingType.THROUGH_ALL, "oppositeDirection" : true, "depth" : 25 * mm, "offsetDistance" : 25 * mm});
        }
        {
            var Q0;
            Q0=makeQuery(id+"F1.opExtrude","SWEPT_FACE",FACE,{"disambiguationData":[OSD([sQuery(id+"F0.wireOp",EDGE,"E8")])]});
            var sketch = newSketch(context, id + "F10", { "sketchPlane" : qUnion([Q0])});
            skLineSegment(sketch, "E47", {"start": v(0, -5.5) * mm, "end": v(-8.31, -14.5) * mm});
            skLineSegment(sketch, "E48", {"start": v(-1340, -5.5) * mm, "end": v(-1331.72, -14.5) * mm});
            skSolve(sketch);
        }
        {
            var Q0;
            {var subQ1=sQuery(id+"F0.wireOp",EDGE,"E8");var subQ6=makeQuery(id+"F1.opExtrude","CAP_EDGE",EDGE,{"disambiguationData":[OSD([subQ1])],"isStart":false});Q0=makeQuery(id+"F10.imprint","IMPRINT",FACE,{"disambiguationData":[TD([[makeQuery(id+"F10.imprint","IMPRINT",EDGE,{"derivedFrom":subQ6}),1.0]])]});}
            var Q1;
            {var subQ0=sQuery(id+"F10.wireOp",EDGE,"E47");Q1=makeQuery(id+"F10.imprint","IMPRINT",FACE,{"disambiguationData":[TD([[makeQuery(id+"F10.imprint","IMPRINT",EDGE,{"derivedFrom":subQ0}),1.0]])]});}
            extrude(context, id + "F11", {"entities" : qUnion([Q0, Q1]), "operationType" : NewBodyOperationType.REMOVE, "endBound" : BoundingType.THROUGH_ALL, "oppositeDirection" : true, "depth" : 25 * mm, "offsetDistance" : 25 * mm});
        }
    });
